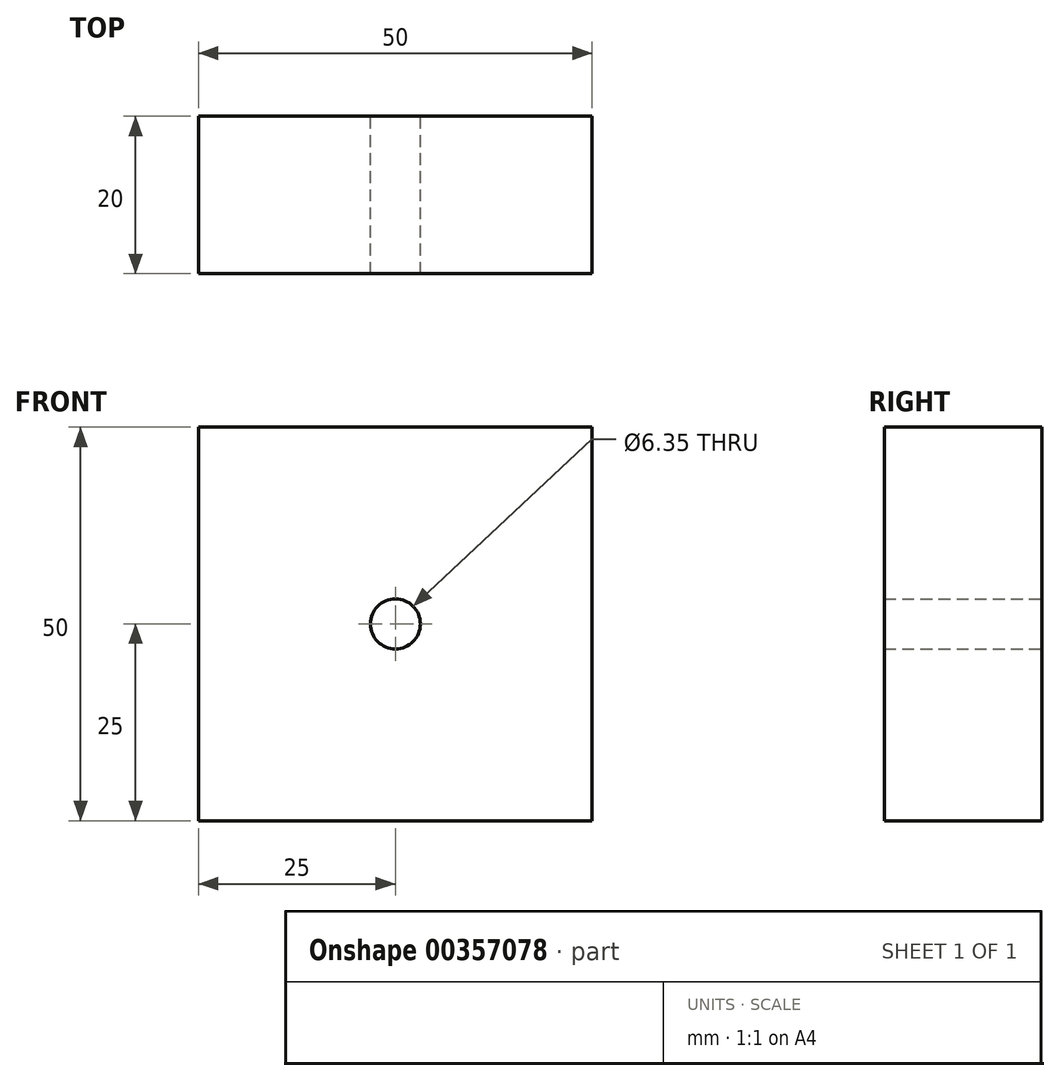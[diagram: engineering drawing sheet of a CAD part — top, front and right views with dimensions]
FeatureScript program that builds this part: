
annotation { "Feature Type Name" : "Feature", "Feature Type Description" : "" }
export const myFeature = defineFeature(function(context is Context, id is Id, definition is map)
    precondition{}
    {
        {
            var Q0;
            Q0=qCreatedBy(makeId("Front.planeOp"),FACE);
            var sketch = newSketch(context, id + "F0", { "sketchPlane" : qUnion([Q0])});
            skLineSegment(sketch, "E0.bottom", {"start": v(25, -25) * mm, "end": v(-25, -25) * mm});
            skLineSegment(sketch, "E0.top", {"start": v(25, 25) * mm, "end": v(-25, 25) * mm});
            skLineSegment(sketch, "E0.left", {"start": v(25, -25) * mm, "end": v(25, 25) * mm});
            skLineSegment(sketch, "E0.right", {"start": v(-25, -25) * mm, "end": v(-25, 25) * mm});
            skPoint(sketch, "E0.middle", {"position": v(0, 0) * mm});
            skCircle(sketch, "E1", {"center": v(0, 0) * mm, "radius": 3.18 * mm});
            skSolve(sketch);
        }
        {
            var Q0;
            Q0=makeQuery(id+"F0.imprint","IMPRINT",FACE,{"disambiguationData":[TD([[makeQuery(id+"F0.imprint","IMPRINT",EDGE,{"derivedFrom":sQuery(id+"F0.wireOp",EDGE,"E0.bottom")}),-1.0]])]});
            extrude(context, id + "F1", {"entities" : qUnion([Q0]), "endBound" : BoundingType.SYMMETRIC, "depth" : 20 * mm});
        }
    });
